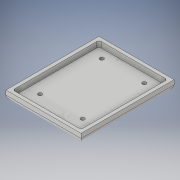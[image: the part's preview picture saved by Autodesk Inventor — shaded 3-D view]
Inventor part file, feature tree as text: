
AUTODESK INVENTOR PART (.ipt)
format: ipt  version: 2019.4 (Build 234330000, 330)  size: 144,384 bytes
history: native  units: mm
features: extrude x3, sketch x3, fillet x2
ambient origin geometry x8: Origin, YZ Plane, XZ Plane, XY Plane, X Axis, Y Axis, Z Axis, Center Point
bodies: Solid1 (feature_tree)
feature tree (8):
  extrude  "Extrusion1"  Depth=83.0mm
  extrude  "Extrusion2"  Depth=61.0mm
  extrude  "Extrusion3"  Depth=5.0mm TaperAngle=0.0deg
  fillet  "Fillet1"  Radius=3.5mm
  fillet  "Fillet2"  Radius=8.0mm
  sketch  "Sketch1"  dims[d0=67.0mm d1=83.0mm]
  sketch  "Sketch2"  dims[d2=3.0mm d3=0.0mm d4=61.0mm]
  sketch  "Sketch3"  dims[d5=77.0mm d6=5.0mm d7=0.0mm d8=3.5mm d9=8.0mm d10=12.5mm d11=20.0mm d13=55.0mm d14=20.0mm d16=38.0mm d19=5.0mm d20=0.0mm d21=4.0mm d22=2.0mm]
